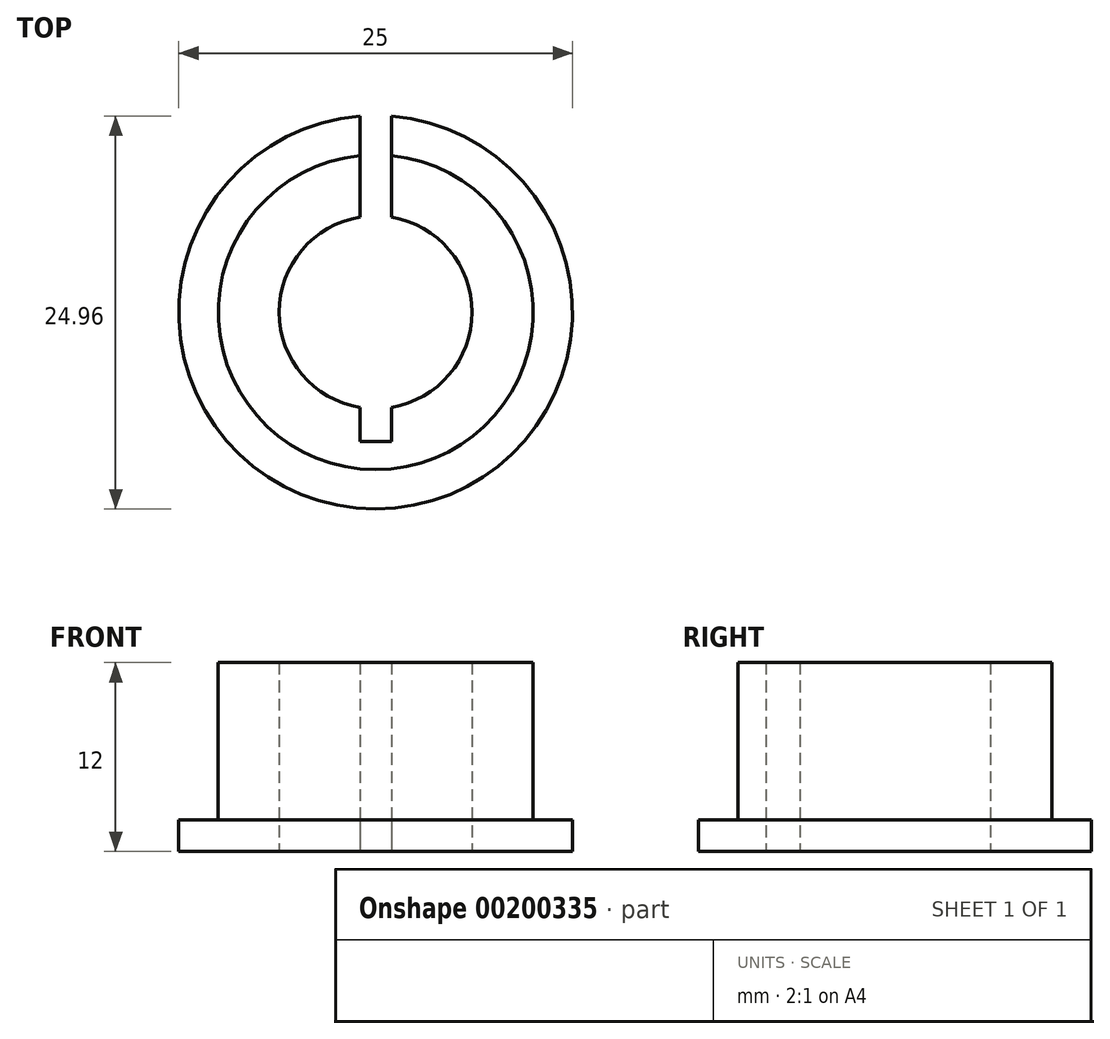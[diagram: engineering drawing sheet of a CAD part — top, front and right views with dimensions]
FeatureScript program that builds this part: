
annotation { "Feature Type Name" : "Feature", "Feature Type Description" : "" }
export const myFeature = defineFeature(function(context is Context, id is Id, definition is map)
    precondition{}
    {
        {
            var Q0;
            Q0=qCreatedBy(makeId("Top.planeOp"),FACE);
            var sketch = newSketch(context, id + "F0", { "sketchPlane" : qUnion([Q0])});
            skCircle(sketch, "E0", {"center": v(-39.16, 0) * mm, "radius": 6.13 * mm});
            skCircle(sketch, "E1", {"center": v(-39.16, 0) * mm, "radius": 10 * mm});
            skLineSegment(sketch, "E2", {"start": v(-39.16, -6.13) * mm, "end": v(-39.16, 6.13) * mm});
            skLineSegment(sketch, "E3.0", {"start": v(-38.16, -6.13) * mm, "end": v(-38.16, 6.13) * mm});
            skLineSegment(sketch, "E4.0", {"start": v(-40.16, -6.22) * mm, "end": v(-40.16, 6.13) * mm});
            skLineSegment(sketch, "E5", {"start": v(-40.16, 6.13) * mm, "end": v(-40.16, 12.46) * mm});
            skLineSegment(sketch, "E6", {"start": v(-38.16, 6.13) * mm, "end": v(-38.16, 12.46) * mm});
            skLineSegment(sketch, "E7", {"start": v(-40.16, -6.22) * mm, "end": v(-40.16, -8.22) * mm});
            skLineSegment(sketch, "E8", {"start": v(-40.16, -8.22) * mm, "end": v(-38.16, -8.22) * mm});
            skLineSegment(sketch, "E9", {"start": v(-38.16, -8.22) * mm, "end": v(-38.16, -6.13) * mm});
            skCircle(sketch, "E10", {"center": v(-39.16, 0) * mm, "radius": 12.5 * mm});
            skSolve(sketch);
        }
        {
            var Q0;
            {var subQ0=sQuery(id+"F0.wireOp",EDGE,"E7");Q0=makeQuery(id+"F0.imprint","IMPRINT",FACE,{"disambiguationData":[TD([[makeQuery(id+"F0.imprint","IMPRINT",EDGE,{"derivedFrom":subQ0}),-1.0]])]});}
            extrude(context, id + "F1", {"entities" : qUnion([Q0]), "depth" : 12 * mm});
        }
        {
            var Q0;
            {var subQ0=sQuery(id+"F0.wireOp",EDGE,"E5");var subQ1=sQuery(id+"F0.wireOp",EDGE,"E1");var subQ2=makeQuery(id+"F0.imprint","INTERSECT",VERTEX,{"derivedFrom":[subQ1,subQ0]});Q0=makeQuery(id+"F0.imprint","IMPRINT",FACE,{"disambiguationData":[TD([[makeQuery(id+"F0.imprint","IMPRINT",EDGE,{"disambiguationData":[TD([[subQ2,-1.0]])],"derivedFrom":subQ1}),-1.0]])]});}
            extrude(context, id + "F2", {"entities" : qUnion([Q0]), "operationType" : NewBodyOperationType.ADD, "depth" : 2 * mm});
        }
    });
